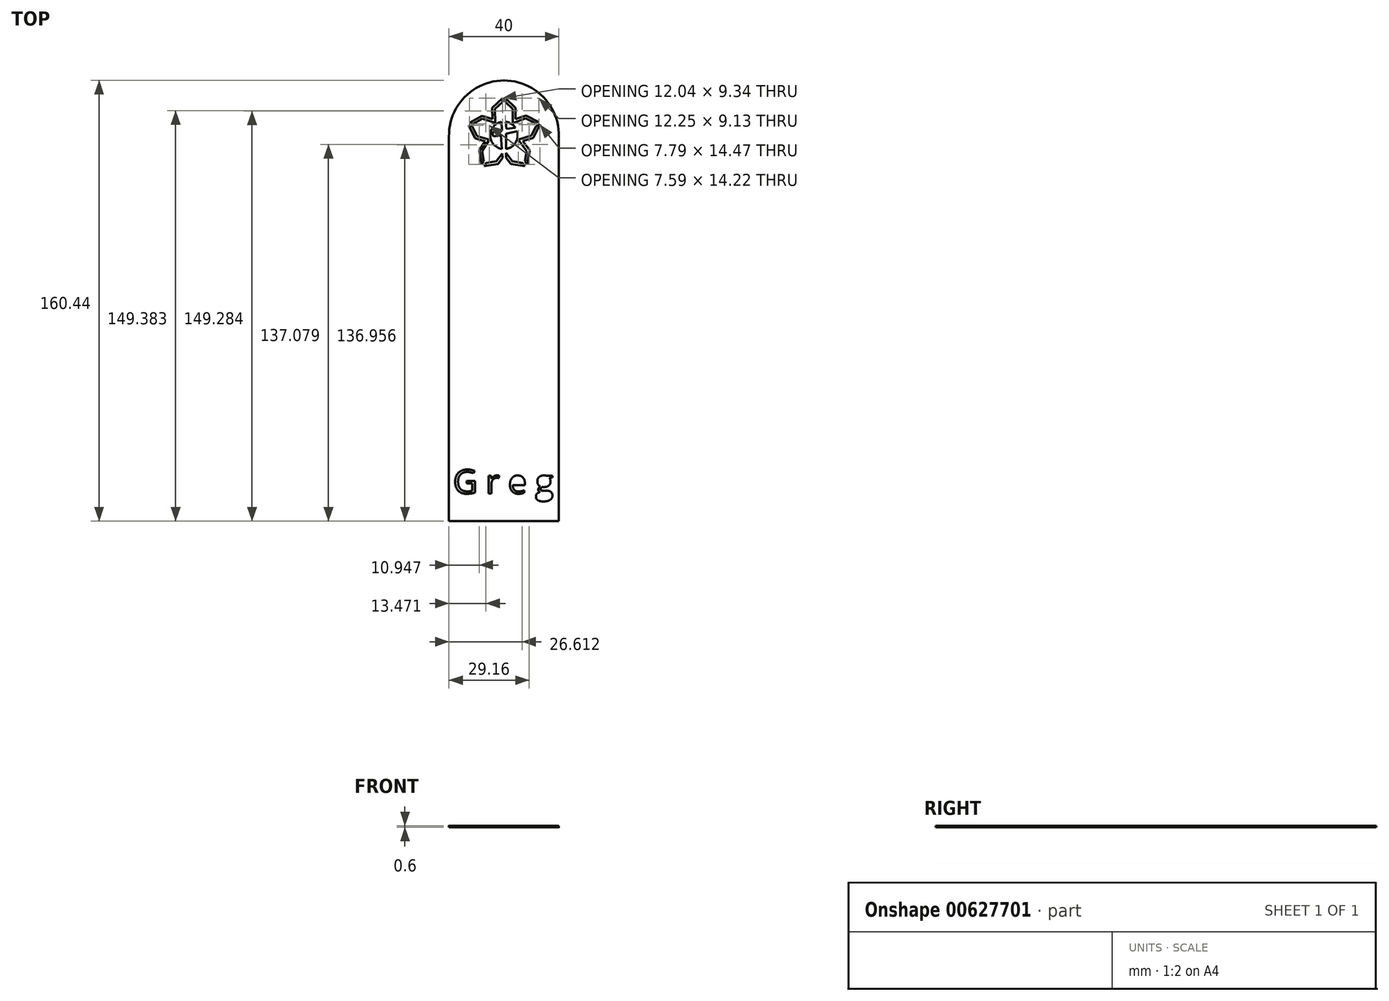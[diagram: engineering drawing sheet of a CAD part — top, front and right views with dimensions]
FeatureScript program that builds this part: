
annotation { "Feature Type Name" : "Feature", "Feature Type Description" : "" }
export const myFeature = defineFeature(function(context is Context, id is Id, definition is map)
    precondition{}
    {
        {
            var Q0;
            Q0=qCreatedBy(makeId("Top.planeOp"),FACE);
            var sketch = newSketch(context, id + "F0", { "sketchPlane" : qUnion([Q0])});
            skLineSegment(sketch, "E0", {"start": v(-29.48, 59.06) * mm, "end": v(-34.17, 60.58) * mm});
            skLineSegment(sketch, "E1", {"start": v(-34.17, 60.58) * mm, "end": v(-37.52, 58.7) * mm});
            skLineSegment(sketch, "E2", {"start": v(-37.82, 57.75) * mm, "end": v(-36.1, 54.29) * mm});
            skLineSegment(sketch, "E3", {"start": v(-36.1, 54.29) * mm, "end": v(-31.55, 52.93) * mm});
            skLineSegment(sketch, "E4", {"start": v(-31.55, 52.93) * mm, "end": v(-34.28, 48.84) * mm});
            skLineSegment(sketch, "E5", {"start": v(-34.28, 48.84) * mm, "end": v(-33.58, 45.07) * mm});
            skLineSegment(sketch, "E6", {"start": v(-32.76, 44.49) * mm, "end": v(-29.04, 45.05) * mm});
            skLineSegment(sketch, "E7", {"start": v(-29.04, 45.05) * mm, "end": v(-26.95, 47.96) * mm});
            skLineSegment(sketch, "E8", {"start": v(-25.5, 48.12) * mm, "end": v(-23.23, 45.05) * mm});
            skLineSegment(sketch, "E9", {"start": v(-23.23, 45.05) * mm, "end": v(-19.49, 44.49) * mm});
            skLineSegment(sketch, "E10", {"start": v(-18.67, 45.07) * mm, "end": v(-17.96, 48.84) * mm});
            skLineSegment(sketch, "E11", {"start": v(-17.96, 48.84) * mm, "end": v(-21.03, 52.93) * mm});
            skLineSegment(sketch, "E12", {"start": v(-21.03, 52.93) * mm, "end": v(-16.27, 54.48) * mm});
            skLineSegment(sketch, "E13", {"start": v(-16.27, 54.48) * mm, "end": v(-14.56, 57.96) * mm});
            skLineSegment(sketch, "E14", {"start": v(-14.88, 58.9) * mm, "end": v(-18.36, 60.69) * mm});
            skLineSegment(sketch, "E15", {"start": v(-18.36, 60.69) * mm, "end": v(-23.1, 59.01) * mm});
            skLineSegment(sketch, "E16", {"start": v(-23.1, 59.01) * mm, "end": v(-23.1, 64.1) * mm});
            skLineSegment(sketch, "E17", {"start": v(-23.1, 64.1) * mm, "end": v(-25.8, 66.67) * mm});
            skLineSegment(sketch, "E18", {"start": v(-26.8, 66.67) * mm, "end": v(-29.59, 64.1) * mm});
            skLineSegment(sketch, "E19", {"start": v(-29.59, 64.1) * mm, "end": v(-29.48, 59.06) * mm});
            skLineSegment(sketch, "E20", {"start": v(-25.39, 56.97) * mm, "end": v(-22.09, 57.24) * mm});
            skLineSegment(sketch, "E21", {"start": v(-25.5, 55.17) * mm, "end": v(-25.5, 49.6) * mm});
            skLineSegment(sketch, "E22", {"start": v(-26.85, 46.39) * mm, "end": v(-26.95, 47.96) * mm});
            skLineSegment(sketch, "E23", {"start": v(-27.36, 54.62) * mm, "end": v(-30.05, 54.08) * mm});
            skLineSegment(sketch, "E24", {"start": v(-30.05, 54.08) * mm, "end": v(-30.74, 55.5) * mm});
            skLineSegment(sketch, "E25", {"start": v(-30.74, 55.5) * mm, "end": v(-27.06, 56.25) * mm});
            skLineSegment(sketch, "E26", {"start": v(-27.06, 56.25) * mm, "end": v(-27.13, 59.46) * mm});
            skArc(sketch, "E27", {"start": v(-6.3, 54.09) * mm, "mid": v(-26.29, 74.53) * mm, "end": v(-46.28, 54.09) * mm});
            skLineSegment(sketch, "E28", {"start": v(-46.28, 54.09) * mm, "end": v(-46.28, -85.91) * mm});
            skLineSegment(sketch, "E29", {"start": v(-6.3, 54.09) * mm, "end": v(-6.3, -85.91) * mm});
            skLineSegment(sketch, "E30", {"start": v(-46.28, -85.91) * mm, "end": v(-6.3, -85.91) * mm});
            skLineSegment(sketch, "E31", {"start": v(-35.33, 49.06) * mm, "end": v(-33.13, 52.36) * mm});
            skLineSegment(sketch, "E32", {"start": v(-35.33, 49.06) * mm, "end": v(-34.39, 43.93) * mm});
            skLineSegment(sketch, "E33", {"start": v(-33.57, 43.35) * mm, "end": v(-28.47, 44.13) * mm});
            skLineSegment(sketch, "E34", {"start": v(-28.47, 44.13) * mm, "end": v(-26.85, 46.39) * mm});
            skLineSegment(sketch, "E35", {"start": v(-25.5, 46.44) * mm, "end": v(-23.79, 44.13) * mm});
            skLineSegment(sketch, "E36", {"start": v(-23.79, 44.13) * mm, "end": v(-18.68, 43.36) * mm});
            skLineSegment(sketch, "E37", {"start": v(-16.9, 49.09) * mm, "end": v(-17.87, 43.93) * mm});
            skLineSegment(sketch, "E38", {"start": v(-19.39, 52.41) * mm, "end": v(-16.9, 49.09) * mm});
            skLineSegment(sketch, "E39", {"start": v(-19.39, 52.41) * mm, "end": v(-15.56, 53.66) * mm});
            skLineSegment(sketch, "E40", {"start": v(-13.23, 58.4) * mm, "end": v(-15.56, 53.66) * mm});
            skLineSegment(sketch, "E41", {"start": v(-18.3, 61.77) * mm, "end": v(-13.55, 59.35) * mm});
            skLineSegment(sketch, "E42", {"start": v(-22.1, 60.43) * mm, "end": v(-18.3, 61.77) * mm});
            skLineSegment(sketch, "E43", {"start": v(-30.6, 64.53) * mm, "end": v(-26.8, 68.04) * mm});
            skLineSegment(sketch, "E44", {"start": v(-30.6, 64.53) * mm, "end": v(-30.5, 60.44) * mm});
            skLineSegment(sketch, "E45", {"start": v(-25.8, 68.04) * mm, "end": v(-22.1, 64.53) * mm});
            skLineSegment(sketch, "E46", {"start": v(-34.28, 61.66) * mm, "end": v(-30.5, 60.44) * mm});
            skLineSegment(sketch, "E47", {"start": v(-38.84, 59.11) * mm, "end": v(-34.28, 61.66) * mm});
            skLineSegment(sketch, "E48", {"start": v(-39.14, 58.16) * mm, "end": v(-36.8, 53.45) * mm});
            skLineSegment(sketch, "E49", {"start": v(-36.8, 53.45) * mm, "end": v(-33.13, 52.36) * mm});
            skLineSegment(sketch, "E50", {"start": v(-38.84, 59.11) * mm, "end": v(-37.52, 58.7) * mm});
            skLineSegment(sketch, "E51", {"start": v(-39.14, 58.16) * mm, "end": v(-37.82, 57.75) * mm});
            skLineSegment(sketch, "E52", {"start": v(-33.57, 43.35) * mm, "end": v(-32.76, 44.49) * mm});
            skLineSegment(sketch, "E53", {"start": v(-34.39, 43.93) * mm, "end": v(-33.58, 45.07) * mm});
            skLineSegment(sketch, "E54", {"start": v(-18.68, 43.36) * mm, "end": v(-19.49, 44.49) * mm});
            skLineSegment(sketch, "E55", {"start": v(-18.67, 45.07) * mm, "end": v(-17.87, 43.93) * mm});
            skLineSegment(sketch, "E56", {"start": v(-25.8, 68.04) * mm, "end": v(-25.8, 66.67) * mm});
            skLineSegment(sketch, "E57", {"start": v(-26.8, 68.04) * mm, "end": v(-26.8, 66.67) * mm});
            skLineSegment(sketch, "E58", {"start": v(-14.88, 58.9) * mm, "end": v(-13.55, 59.35) * mm});
            skLineSegment(sketch, "E59", {"start": v(-14.56, 57.96) * mm, "end": v(-13.23, 58.4) * mm});
            skLineSegment(sketch, "E60.trimOffspring", {"start": v(-22.1, 60.43) * mm, "end": v(-22.1, 64.53) * mm});
            skArc(sketch, "E61", {"start": v(-25.5, 49.6) * mm, "mid": v(-22.05, 51.88) * mm, "end": v(-21.5, 55.98) * mm});
            skLineSegment(sketch, "E62.trimOffspring", {"start": v(-27.05, 49.59) * mm, "end": v(-27.36, 54.62) * mm});
            skLineSegment(sketch, "E63.trimOffspring", {"start": v(-25.5, 48.12) * mm, "end": v(-25.5, 46.44) * mm});
            skArc(sketch, "E64.trimOffspring", {"start": v(-22.09, 57.24) * mm, "mid": v(-23.6, 58.75) * mm, "end": v(-25.6, 59.48) * mm});
            skLineSegment(sketch, "E65.trimOffspring", {"start": v(-21.5, 55.98) * mm, "end": v(-25.5, 55.17) * mm});
            skArc(sketch, "E66.trimOffspring", {"start": v(-27.13, 59.46) * mm, "mid": v(-31.29, 54.49) * mm, "end": v(-27.05, 49.59) * mm});
            skLineSegment(sketch, "E67.trimOffspring", {"start": v(-25.6, 59.48) * mm, "end": v(-25.39, 56.97) * mm});
            skSolve(sketch);
        }
        {
            var Q0;
            Q0=makeQuery(id+"F0.imprint","IMPRINT",FACE,{"disambiguationData":[TD([[makeQuery(id+"F0.imprint","IMPRINT",EDGE,{"derivedFrom":sQuery(id+"F0.wireOp",EDGE,"E0")}),1.0]])]});
            extrude(context, id + "F1", {"entities" : qUnion([Q0]), "depth" : .6 * mm, "offsetDistance" : 25 * mm});
        }
        {
            var Q0;
            Q0=makeQuery(id+"F1.opExtrude","CAP_FACE",FACE,{"disambiguationData":[OSD([sQuery(id+"F0.wireOp",EDGE,"E0"),sQuery(id+"F0.wireOp",EDGE,"E1"),sQuery(id+"F0.wireOp",EDGE,"E2"),sQuery(id+"F0.wireOp",EDGE,"E3"),sQuery(id+"F0.wireOp",EDGE,"E4"),sQuery(id+"F0.wireOp",EDGE,"E5"),sQuery(id+"F0.wireOp",EDGE,"E6"),sQuery(id+"F0.wireOp",EDGE,"E7"),sQuery(id+"F0.wireOp",EDGE,"E8"),sQuery(id+"F0.wireOp",EDGE,"E9"),sQuery(id+"F0.wireOp",EDGE,"E10"),sQuery(id+"F0.wireOp",EDGE,"E11"),sQuery(id+"F0.wireOp",EDGE,"E12"),sQuery(id+"F0.wireOp",EDGE,"E13"),sQuery(id+"F0.wireOp",EDGE,"E14"),sQuery(id+"F0.wireOp",EDGE,"E15"),sQuery(id+"F0.wireOp",EDGE,"E16"),sQuery(id+"F0.wireOp",EDGE,"E17"),sQuery(id+"F0.wireOp",EDGE,"E18"),sQuery(id+"F0.wireOp",EDGE,"E19"),sQuery(id+"F0.wireOp",EDGE,"E20"),sQuery(id+"F0.wireOp",EDGE,"E21"),sQuery(id+"F0.wireOp",EDGE,"E22"),sQuery(id+"F0.wireOp",EDGE,"E23"),sQuery(id+"F0.wireOp",EDGE,"E24"),sQuery(id+"F0.wireOp",EDGE,"E25"),sQuery(id+"F0.wireOp",EDGE,"E26"),sQuery(id+"F0.wireOp",EDGE,"E27"),sQuery(id+"F0.wireOp",EDGE,"E28"),sQuery(id+"F0.wireOp",EDGE,"E29"),sQuery(id+"F0.wireOp",EDGE,"E30"),sQuery(id+"F0.wireOp",EDGE,"E31"),sQuery(id+"F0.wireOp",EDGE,"E32"),sQuery(id+"F0.wireOp",EDGE,"E33"),sQuery(id+"F0.wireOp",EDGE,"E34"),sQuery(id+"F0.wireOp",EDGE,"E35"),sQuery(id+"F0.wireOp",EDGE,"E36"),sQuery(id+"F0.wireOp",EDGE,"E37"),sQuery(id+"F0.wireOp",EDGE,"E38"),sQuery(id+"F0.wireOp",EDGE,"E39"),sQuery(id+"F0.wireOp",EDGE,"E40"),sQuery(id+"F0.wireOp",EDGE,"E41"),sQuery(id+"F0.wireOp",EDGE,"E42"),sQuery(id+"F0.wireOp",EDGE,"E43"),sQuery(id+"F0.wireOp",EDGE,"E44"),sQuery(id+"F0.wireOp",EDGE,"E45"),sQuery(id+"F0.wireOp",EDGE,"E46"),sQuery(id+"F0.wireOp",EDGE,"E47"),sQuery(id+"F0.wireOp",EDGE,"E48"),sQuery(id+"F0.wireOp",EDGE,"E49"),sQuery(id+"F0.wireOp",EDGE,"E50"),sQuery(id+"F0.wireOp",EDGE,"E51"),sQuery(id+"F0.wireOp",EDGE,"E52"),sQuery(id+"F0.wireOp",EDGE,"E53"),sQuery(id+"F0.wireOp",EDGE,"E54"),sQuery(id+"F0.wireOp",EDGE,"E55"),sQuery(id+"F0.wireOp",EDGE,"E56"),sQuery(id+"F0.wireOp",EDGE,"E57"),sQuery(id+"F0.wireOp",EDGE,"E58"),sQuery(id+"F0.wireOp",EDGE,"E59"),sQuery(id+"F0.wireOp",EDGE,"E60.trimOffspring"),sQuery(id+"F0.wireOp",EDGE,"E61"),sQuery(id+"F0.wireOp",EDGE,"E62.trimOffspring"),sQuery(id+"F0.wireOp",EDGE,"E63.trimOffspring"),sQuery(id+"F0.wireOp",EDGE,"E64.trimOffspring"),sQuery(id+"F0.wireOp",EDGE,"E65.trimOffspring"),sQuery(id+"F0.wireOp",EDGE,"E66.trimOffspring"),sQuery(id+"F0.wireOp",EDGE,"E67.trimOffspring")])],"isStart":false});
            var sketch = newSketch(context, id + "F2", { "sketchPlane" : qUnion([Q0])});
            skText(sketch, "E68", { "text": "G r e g", "fontName": "OpenSans-Regular.ttf"});
            const initialGuessF2  = {"E68": [-0.04478, -0.07591, 1, 0, 0.00869]};
            skSetInitialGuess(sketch, initialGuessF2);
            skSolve(sketch);
        }
        {
            var Q0;
            Q0=makeQuery(id+"F2.imprint","IMPRINT",FACE,{"disambiguationData":[TD([[makeQuery(id+"F2.imprint","IMPRINT",EDGE,{"derivedFrom":sQuery(id+"F2.wireOp",EDGE,"E68.sketch_text.stroke-0")}),-1.0]])]});
            var Q1;
            Q1=makeQuery(id+"F2.imprint","IMPRINT",FACE,{"disambiguationData":[TD([[makeQuery(id+"F2.imprint","IMPRINT",EDGE,{"derivedFrom":sQuery(id+"F2.wireOp",EDGE,"E68.sketch_text.stroke-20")}),-1.0]])]});
            var Q2;
            Q2=makeQuery(id+"F2.imprint","IMPRINT",FACE,{"disambiguationData":[TD([[makeQuery(id+"F2.imprint","IMPRINT",EDGE,{"derivedFrom":sQuery(id+"F2.wireOp",EDGE,"E68.sketch_text.stroke-90")}),1.0]])]});
            var Q3;
            Q3=makeQuery(id+"F2.imprint","IMPRINT",FACE,{"disambiguationData":[TD([[makeQuery(id+"F2.imprint","IMPRINT",EDGE,{"derivedFrom":sQuery(id+"F2.wireOp",EDGE,"E68.sketch_text.stroke-81")}),1.0]])]});
            var Q4;
            Q4=makeQuery(id+"F2.imprint","IMPRINT",FACE,{"disambiguationData":[TD([[makeQuery(id+"F2.imprint","IMPRINT",EDGE,{"derivedFrom":sQuery(id+"F2.wireOp",EDGE,"E68.sketch_text.stroke-52")}),-1.0]])]});
            var Q5;
            Q5=makeQuery(id+"F2.imprint","IMPRINT",FACE,{"disambiguationData":[TD([[makeQuery(id+"F2.imprint","IMPRINT",EDGE,{"derivedFrom":sQuery(id+"F2.wireOp",EDGE,"E68.sketch_text.stroke-33")}),-1.0]])]});
            var Q6;
            Q6=makeQuery(id+"F2.imprint","IMPRINT",FACE,{"disambiguationData":[TD([[makeQuery(id+"F2.imprint","IMPRINT",EDGE,{"derivedFrom":sQuery(id+"F2.wireOp",EDGE,"E68.sketch_text.stroke-47")}),1.0]])]});
            extrude(context, id + "F3", {"entities" : qUnion([Q0, Q1, Q2, Q3, Q4, Q5, Q6]), "operationType" : NewBodyOperationType.REMOVE, "oppositeDirection" : true, "depth" : 25 * mm, "offsetDistance" : 25 * mm});
        }
    });
